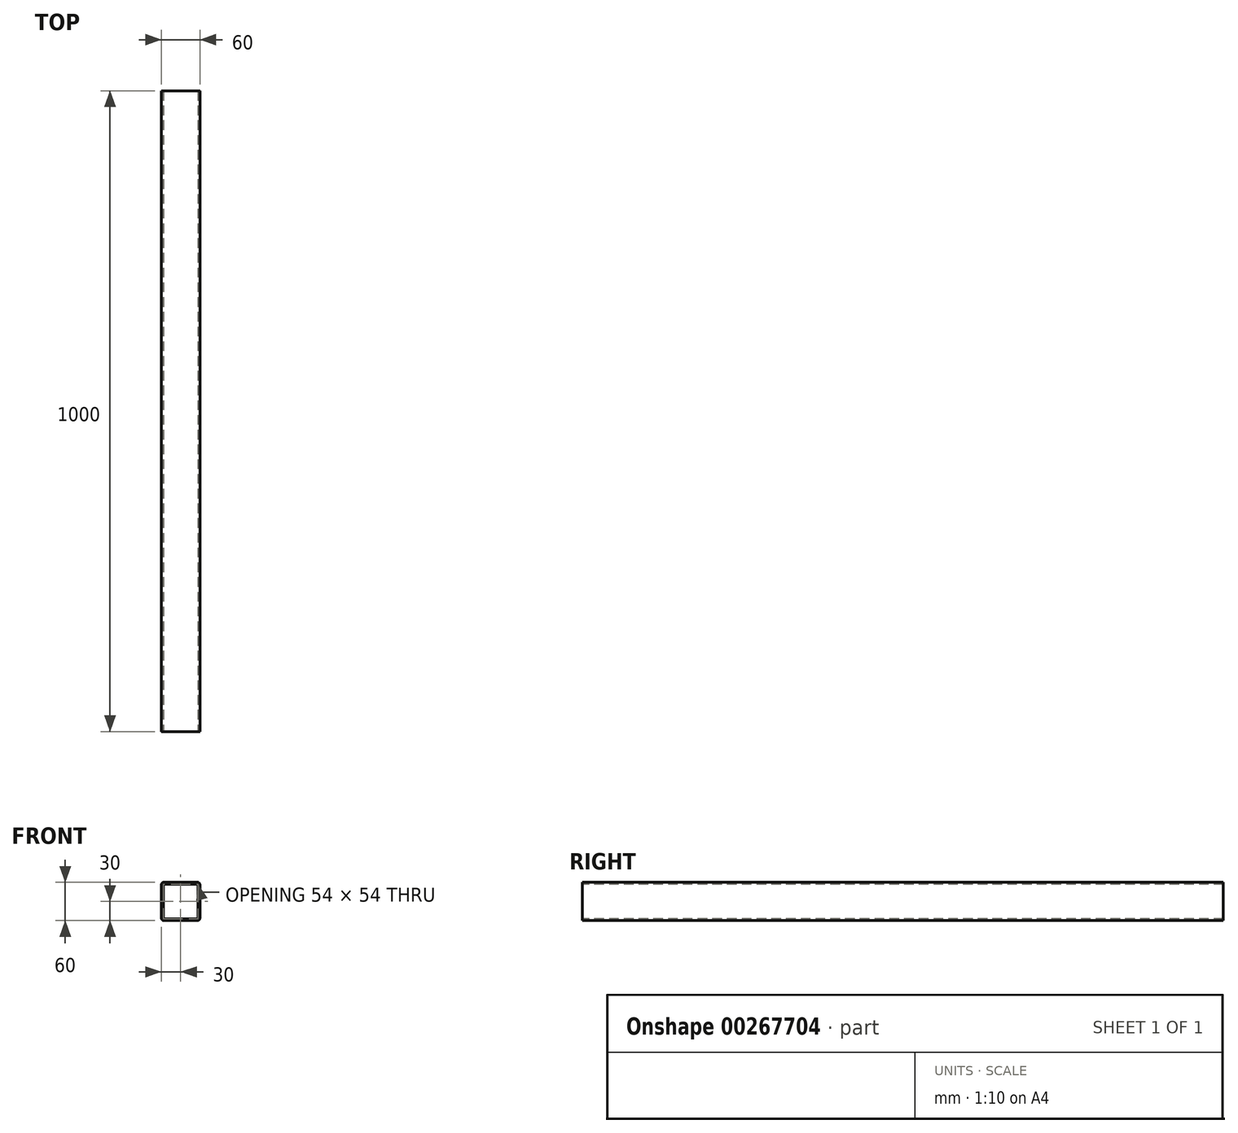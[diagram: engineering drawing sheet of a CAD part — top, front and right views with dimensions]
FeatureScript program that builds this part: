
annotation { "Feature Type Name" : "Feature", "Feature Type Description" : "" }
export const myFeature = defineFeature(function(context is Context, id is Id, definition is map)
    precondition{}
    {
        {
            var Q0;
            Q0=qCreatedBy(makeId("Front.planeOp"),FACE);
            var sketch = newSketch(context, id + "F0", { "sketchPlane" : qUnion([Q0])});
            skLineSegment(sketch, "E0.bottom", {"start": v(26, -30) * mm, "end": v(-26, -30) * mm});
            skLineSegment(sketch, "E0.top", {"start": v(26, 30) * mm, "end": v(-26, 30) * mm});
            skLineSegment(sketch, "E0.left", {"start": v(30, -26) * mm, "end": v(30, 26) * mm});
            skLineSegment(sketch, "E0.right", {"start": v(-30, -26) * mm, "end": v(-30, 26) * mm});
            skPoint(sketch, "E0.middle", {"position": v(0, 0) * mm});
            skPoint(sketch, "E1.visualSharp", {"position": v(-30, 30) * mm});
            skArc(sketch, "E1.filletArc", {"start": v(-26, 30) * mm, "mid": v(-28.83, 28.83) * mm, "end": v(-30, 26) * mm});
            skPoint(sketch, "E2.visualSharp", {"position": v(30, 30) * mm});
            skArc(sketch, "E2.filletArc", {"start": v(30, 26) * mm, "mid": v(28.83, 28.83) * mm, "end": v(26, 30) * mm});
            skPoint(sketch, "E3.visualSharp", {"position": v(30, -30) * mm});
            skArc(sketch, "E3.filletArc", {"start": v(26, -30) * mm, "mid": v(28.83, -28.83) * mm, "end": v(30, -26) * mm});
            skPoint(sketch, "E4.visualSharp", {"position": v(-30, -30) * mm});
            skArc(sketch, "E4.filletArc", {"start": v(-30, -26) * mm, "mid": v(-28.83, -28.83) * mm, "end": v(-26, -30) * mm});
            skArc(sketch, "E5.0", {"start": v(-27, -26) * mm, "mid": v(-26.7, -26.7) * mm, "end": v(-26, -27) * mm});
            skLineSegment(sketch, "E5.1", {"start": v(26, -27) * mm, "end": v(-26, -27) * mm});
            skLineSegment(sketch, "E5.2", {"start": v(-27, -26) * mm, "end": v(-27, 26) * mm});
            skArc(sketch, "E5.3", {"start": v(26, -27) * mm, "mid": v(26.7, -26.7) * mm, "end": v(27, -26) * mm});
            skArc(sketch, "E5.4", {"start": v(-26, 27) * mm, "mid": v(-26.7, 26.7) * mm, "end": v(-27, 26) * mm});
            skLineSegment(sketch, "E5.5", {"start": v(26, 27) * mm, "end": v(-26, 27) * mm});
            skArc(sketch, "E5.6", {"start": v(27, 26) * mm, "mid": v(26.7, 26.7) * mm, "end": v(26, 27) * mm});
            skLineSegment(sketch, "E5.7", {"start": v(27, -26) * mm, "end": v(27, 26) * mm});
            skSolve(sketch);
        }
        {
            var Q0;
            Q0=qSketchRegion(id+"F0",true);
            extrude(context, id + "F1", {"entities" : qUnion([Q0]), "oppositeDirection" : true, "depth" : 1000 * mm});
        }
    });
